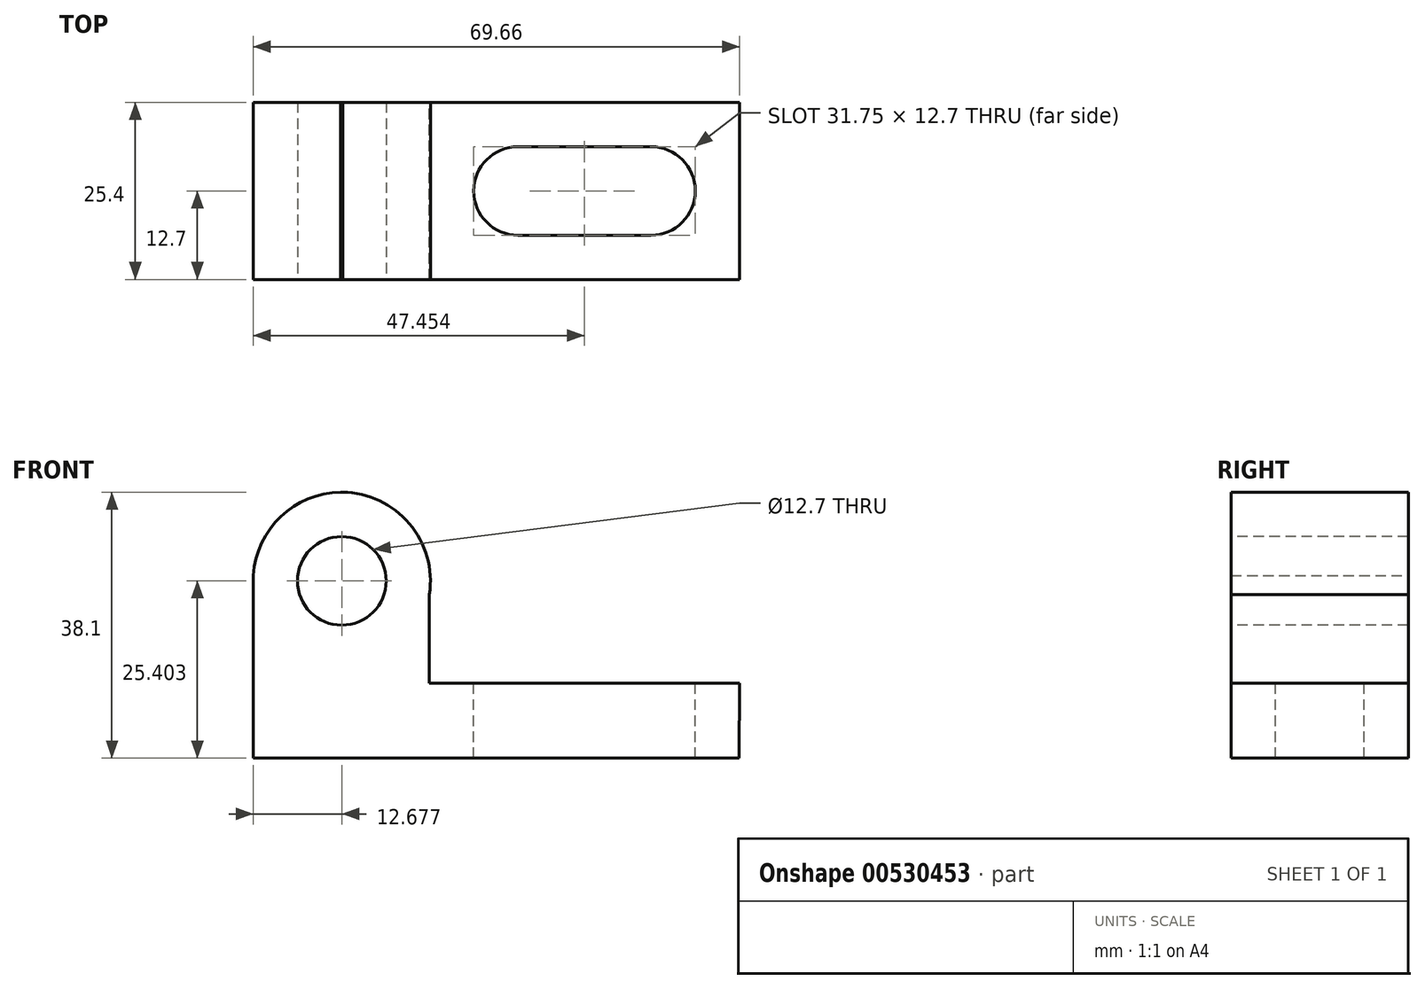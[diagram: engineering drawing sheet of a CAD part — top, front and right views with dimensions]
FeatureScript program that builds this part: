
annotation { "Feature Type Name" : "Feature", "Feature Type Description" : "" }
export const myFeature = defineFeature(function(context is Context, id is Id, definition is map)
    precondition{}
    {
        {
            var Q0;
            Q0=qCreatedBy(makeId("Front.planeOp"),FACE);
            var sketch = newSketch(context, id + "F0", { "sketchPlane" : qUnion([Q0])});
            skLineSegment(sketch, "E0", {"start": v(-58.05, 16.45) * mm, "end": v(11.8, 16.45) * mm});
            skLineSegment(sketch, "E1", {"start": v(11.8, 16.45) * mm, "end": v(11.8, 54.55) * mm});
            skLineSegment(sketch, "E2", {"start": v(11.8, 54.55) * mm, "end": v(-57.8, 54.55) * mm});
            skLineSegment(sketch, "E3", {"start": v(-57.8, 54.55) * mm, "end": v(-58.05, 16.45) * mm});
            skSolve(sketch);
        }
        {
            var Q0;
            Q0=makeQuery(id+"F0.imprint","IMPRINT",FACE,{"disambiguationData":[TD([[makeQuery(id+"F0.imprint","IMPRINT",EDGE,{"derivedFrom":sQuery(id+"F0.wireOp",EDGE,"E0")}),1.0]])]});
            var sketch = newSketch(context, id + "F1", { "sketchPlane" : qUnion([Q0])});
            skLineSegment(sketch, "E4", {"start": v(-32.65, 39.92) * mm, "end": v(11.85, 39.92) * mm});
            skArc(sketch, "E5", {"start": v(-32.65, 39.92) * mm, "mid": v(-43.84, 54.48) * mm, "end": v(-57.88, 42.63) * mm});
            skLineSegment(sketch, "E6", {"start": v(-57.88, 42.63) * mm, "end": v(-57.88, 16.2) * mm});
            skLineSegment(sketch, "E7", {"start": v(-57.88, 16.2) * mm, "end": v(11.71, 16.2) * mm});
            skLineSegment(sketch, "E8", {"start": v(11.71, 16.2) * mm, "end": v(11.85, 39.92) * mm});
            skSolve(sketch);
        }
        {
            var Q0;
            {var subQ1=sQuery(id+"F1.wireOp",EDGE,"E5");var subQ5=sQuery(id+"F1.wireOp",EDGE,"E4");var subQ6=makeQuery(id+"F1.imprint","INTERSECT",VERTEX,{"derivedFrom":[subQ5,subQ1]});Q0=makeQuery(id+"F1.imprint","IMPRINT",FACE,{"disambiguationData":[TD([[makeQuery(id+"F1.imprint","IMPRINT",EDGE,{"disambiguationData":[TD([[subQ6,-1.0]])],"derivedFrom":subQ5}),-1.0]])]});}
            extrude(context, id + "F2", {"entities" : qUnion([Q0]), "depth" : 25.4 * mm, "offsetDistance" : 25.4 * mm});
        }
        {
            var Q0;
            Q0=makeQuery(id+"F2.opExtrude","CAP_FACE",FACE,{"disambiguationData":[OSD([sQuery(id+"F0.wireOp",EDGE,"E0"),sQuery(id+"F0.wireOp",EDGE,"E1"),sQuery(id+"F0.wireOp",EDGE,"E2"),sQuery(id+"F1.wireOp",EDGE,"E4"),sQuery(id+"F1.wireOp",EDGE,"E5"),sQuery(id+"F1.wireOp",EDGE,"E6"),sQuery(id+"F1.wireOp",EDGE,"E8")])],"isStart":false});
            var sketch = newSketch(context, id + "F3", { "sketchPlane" : qUnion([Q0])});
            skCircle(sketch, "E9", {"center": v(-45.2, 41.85) * mm, "radius": 6.35 * mm});
            skSolve(sketch);
        }
        {
            var Q0;
            Q0=makeQuery(id+"F3.imprint","IMPRINT",FACE,{"disambiguationData":[TD([[makeQuery(id+"F3.imprint","IMPRINT",EDGE,{"derivedFrom":sQuery(id+"F3.wireOp",EDGE,"E9")}),1.0]])]});
            extrude(context, id + "F4", {"entities" : qUnion([Q0]), "operationType" : NewBodyOperationType.REMOVE, "endBound" : BoundingType.THROUGH_ALL, "oppositeDirection" : true, "depth" : 25.4 * mm, "offsetDistance" : 25.4 * mm});
        }
        {
            var Q0;
            Q0=makeQuery(id+"F2.opExtrude","SWEPT_FACE",FACE,{"disambiguationData":[OSD([sQuery(id+"F1.wireOp",EDGE,"E4")])]});
            var sketch = newSketch(context, id + "F5", { "sketchPlane" : qUnion([Q0])});
            skCircle(sketch, "E10", {"center": v(-0.9, -12.7) * mm, "radius": 6.35 * mm});
            skCircle(sketch, "E11", {"center": v(-19.95, -12.7) * mm, "radius": 6.35 * mm});
            skLineSegment(sketch, "E12", {"start": v(-19.95, -12.7) * mm, "end": v(-19.95, -6.35) * mm});
            skLineSegment(sketch, "E13", {"start": v(-19.95, -6.35) * mm, "end": v(-0.9, -6.35) * mm});
            skLineSegment(sketch, "E14", {"start": v(-0.9, -6.35) * mm, "end": v(-0.9, -12.7) * mm});
            skLineSegment(sketch, "E15", {"start": v(-0.9, -19.05) * mm, "end": v(-19.95, -19.05) * mm});
            skLineSegment(sketch, "E16", {"start": v(-19.95, -19.05) * mm, "end": v(-19.95, -12.7) * mm});
            skSolve(sketch);
        }
        {
            var Q0;
            {var subQ0=sQuery(id+"F5.wireOp",EDGE,"E12");Q0=makeQuery(id+"F5.imprint","IMPRINT",FACE,{"disambiguationData":[TD([[makeQuery(id+"F5.imprint","IMPRINT",EDGE,{"derivedFrom":subQ0}),1.0]])]});}
            var Q1;
            {var subQ0=sQuery(id+"F5.wireOp",EDGE,"E12");Q1=makeQuery(id+"F5.imprint","IMPRINT",FACE,{"disambiguationData":[TD([[makeQuery(id+"F5.imprint","IMPRINT",EDGE,{"derivedFrom":subQ0}),-1.0]])]});}
            var Q2;
            {var subQ0=sQuery(id+"F5.wireOp",EDGE,"E13");Q2=makeQuery(id+"F5.imprint","IMPRINT",FACE,{"disambiguationData":[TD([[makeQuery(id+"F5.imprint","IMPRINT",EDGE,{"derivedFrom":subQ0}),-1.0]])]});}
            var Q3;
            {var subQ0=sQuery(id+"F5.wireOp",EDGE,"E10");var subQ1=makeQuery(id+"F5.imprint","INTERSECT",VERTEX,{"derivedFrom":[subQ0,sQuery(id+"F5.wireOp",EDGE,"E13")]});Q3=makeQuery(id+"F5.imprint","IMPRINT",FACE,{"disambiguationData":[TD([[makeQuery(id+"F5.imprint","IMPRINT",EDGE,{"disambiguationData":[TD([[subQ1,-1.0]])],"derivedFrom":subQ0}),1.0]])]});}
            extrude(context, id + "F6", {"entities" : qUnion([Q0, Q1, Q2, Q3]), "operationType" : NewBodyOperationType.REMOVE, "endBound" : BoundingType.THROUGH_ALL, "oppositeDirection" : true, "depth" : 25.4 * mm, "offsetDistance" : 25.4 * mm});
        }
        {
            var Q0;
            Q0=makeQuery(id+"F2.opExtrude","SWEPT_FACE",FACE,{"disambiguationData":[OSD([sQuery(id+"F1.wireOp",EDGE,"E4")])]});
            var sketch = newSketch(context, id + "F7", { "sketchPlane" : qUnion([Q0])});
            skLineSegment(sketch, "E17", {"start": v(-32.65, 0) * mm, "end": v(11.8, 0) * mm});
            skLineSegment(sketch, "E18", {"start": v(11.8, 0) * mm, "end": v(11.8, -25.4) * mm});
            skLineSegment(sketch, "E19", {"start": v(11.8, -25.4) * mm, "end": v(-32.65, -25.4) * mm});
            skLineSegment(sketch, "E20", {"start": v(-32.65, -25.4) * mm, "end": v(-32.65, 0) * mm});
            skSolve(sketch);
        }
        {
            var Q0;
            Q0 = qSketchRegion(id + "F7", true);
            extrude(context, id + "F8", {"entities" : qUnion([Q0]), "operationType" : NewBodyOperationType.REMOVE, "oppositeDirection" : true, "depth" : 12.7 * mm, "offsetDistance" : 25.4 * mm});
        }
    });
